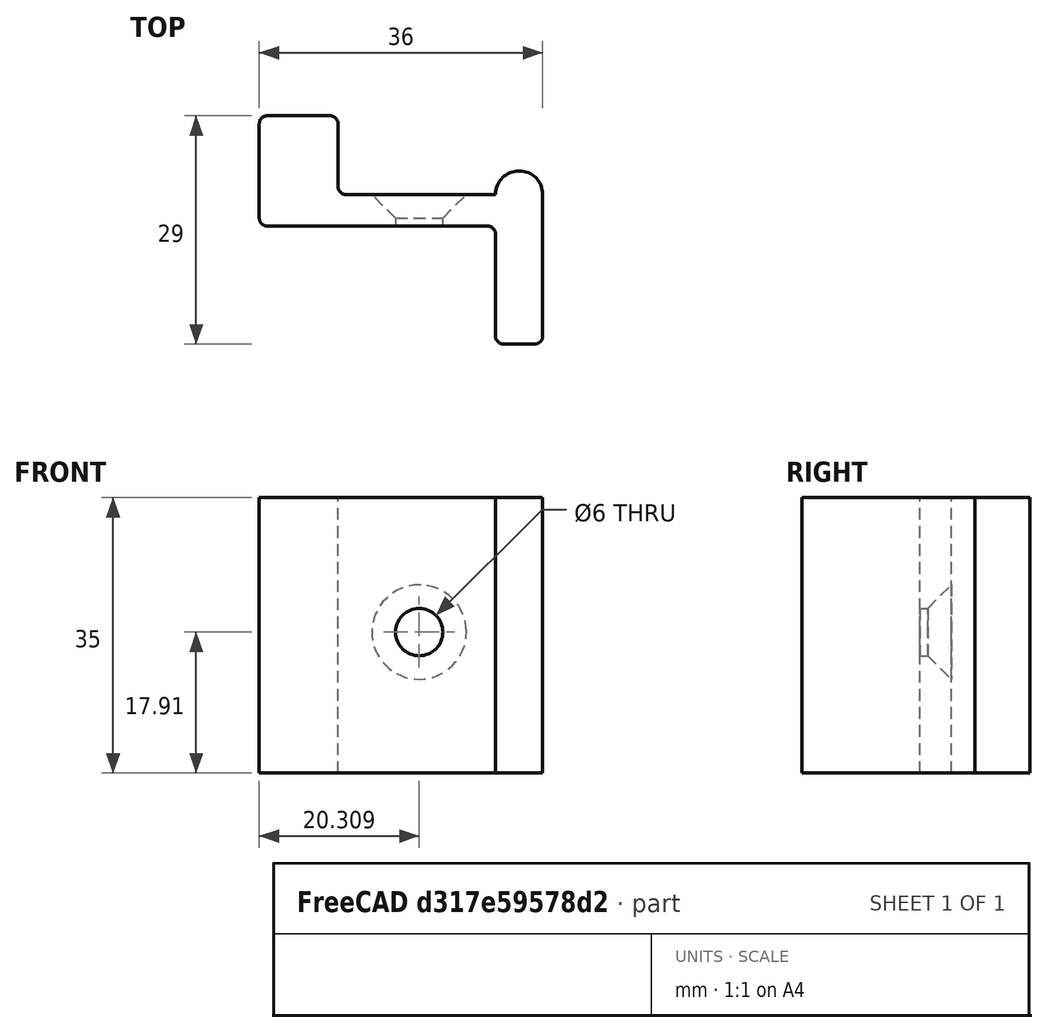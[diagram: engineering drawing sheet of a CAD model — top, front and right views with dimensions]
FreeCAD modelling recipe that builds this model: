
FCSTD DOCUMENT  (FreeCAD 0.19R)
Label: FurnaceStopper
License: All rights reserved
LicenseURL: http://en.wikipedia.org/wiki/All_rights_reserved
objects: Sketcher::SketchObject×3, PartDesign::Pad×2, PartDesign::Pocket×1, PartDesign::Chamfer×1, PartDesign::Fillet×1, PartDesign::Body×1, Mesh::Feature×1
note: 14 computed .brp shape members not serialized (recipe doc carries the construction recipe); baked Part::Feature solids carry a one-line shape summary decoded from their .brp

FEATURE [Sketcher::SketchObject] Sketch
  FullyConstrained = true
  MapMode = 5
  Support = -> [XY_Plane]
  sketch-geometry (8):
    g0: LineSegment StartX=0 StartY=0 StartZ=0 EndX=30 EndY=0 EndZ=0
    g1: LineSegment StartX=30 StartY=0 StartZ=0 EndX=30 EndY=-15 EndZ=0
    g2: LineSegment StartX=30 StartY=-15 StartZ=0 EndX=36 EndY=-15 EndZ=0
    g3: LineSegment StartX=36 StartY=-15 StartZ=0 EndX=36 EndY=4 EndZ=0
    g4: LineSegment StartX=36 StartY=4 StartZ=0 EndX=10 EndY=4 EndZ=0
    g5: LineSegment StartX=10 StartY=4 StartZ=0 EndX=10 EndY=14 EndZ=0
    g6: LineSegment StartX=10 StartY=14 StartZ=0 EndX=0 EndY=14 EndZ=0
    g7: LineSegment StartX=0 StartY=14 StartZ=0 EndX=0 EndY=0 EndZ=0
  constraints (23):
    c: Coincident(g-1,g0)
    c: PointOnObject(g0,g-1)
    c: Coincident(g0,g1)
    c: Vertical(g1)
    c: Coincident(g1,g2)
    c: Coincident(g2,g3)
    c: Vertical(g3)
    c: Coincident(g3,g4)
    c: Horizontal(g4)
    c: Distance(g2) = 6
    c: Horizontal(g2)
    c: DistanceY(g1,g1) = 15
    c: Distance(g4) = 26
    c: Coincident(g4,g5)
    c: Coincident(g5,g6)
    c: PointOnObject(g6,g-2)
    c: Horizontal(g6)
    c: Coincident(g6,g7)
    c: Coincident(g7,g0)
    c: Vertical(g5)
    c: Distance(g6) = 10
    c: Distance(g5) = 10
    c: DistanceY(g3) = 4
FEATURE [PartDesign::Pad] Pad
  Direction = (1,1,1)
  Length = 35
  Length2 = 100
  Profile = -> Sketch
  Type = 0
FEATURE [Sketcher::SketchObject] Sketch001
  ExternalGeometry = -> [Pad]
  FullyConstrained = true
  MapMode = 5
  Placement = pos=(0,0,35) rot=(0,0,1;0rad)
  Support = -> [Pad]
  sketch-geometry (1):
    g0: Circle CenterX=33 CenterY=4 CenterZ=0 NormalX=0 NormalY=0 NormalZ=1 AngleXU=0 Radius=3
  constraints (3):
    c: Diameter(g0) = 6
    c: PointOnObject(g0,g-3)
    c: Tangent(g0,g-4)
FEATURE [PartDesign::Pad] Pad001
  BaseFeature = -> Pad
  Direction = (1,1,1)
  Length = 35
  Length2 = 100
  Profile = -> Sketch001
  Reversed = true
  Type = 0
FEATURE [Sketcher::SketchObject] Sketch002
  FullyConstrained = false
  MapMode = 5
  Placement = pos=(0,4,0) rot=(0,0.707107,0.707107;3.14159rad)
  Support = -> [Pad001]
  sketch-geometry (1):
    g0: Circle CenterX=-20.3094 CenterY=17.9104 CenterZ=0 NormalX=0 NormalY=0 NormalZ=1 AngleXU=0 Radius=3
  constraints (1):
    c: Diameter(g0) = 6
FEATURE [PartDesign::Pocket] Pocket
  BaseFeature = -> Pad001
  Length = 5
  Length2 = 100
  Profile = -> Sketch002
  Type = 1
FEATURE [PartDesign::Chamfer] Chamfer
  Angle = 45
  Base = -> Pocket [Edge24]
  BaseFeature = -> Pocket
  ChamferType = 0
  FlipDirection = false
  Size = 3
  Size2 = 1
  SupportTransform = false
FEATURE [PartDesign::Fillet] Fillet
  Base = -> Chamfer [Edge35,Edge29,Edge9,Edge6,Edge14,Edge33,Edge12]
  BaseFeature = -> Chamfer
  Radius = 1
  SupportTransform = false
FEATURE [PartDesign::Body] Body
  Group = -> [Sketch,Pad,Sketch001,Pad001,Sketch002,Pocket,Chamfer,Fillet]
  Origin = -> Origin
  Tip = -> Fillet
FEATURE [Mesh::Feature] Mesh  label="Fillet (Meshed)"
